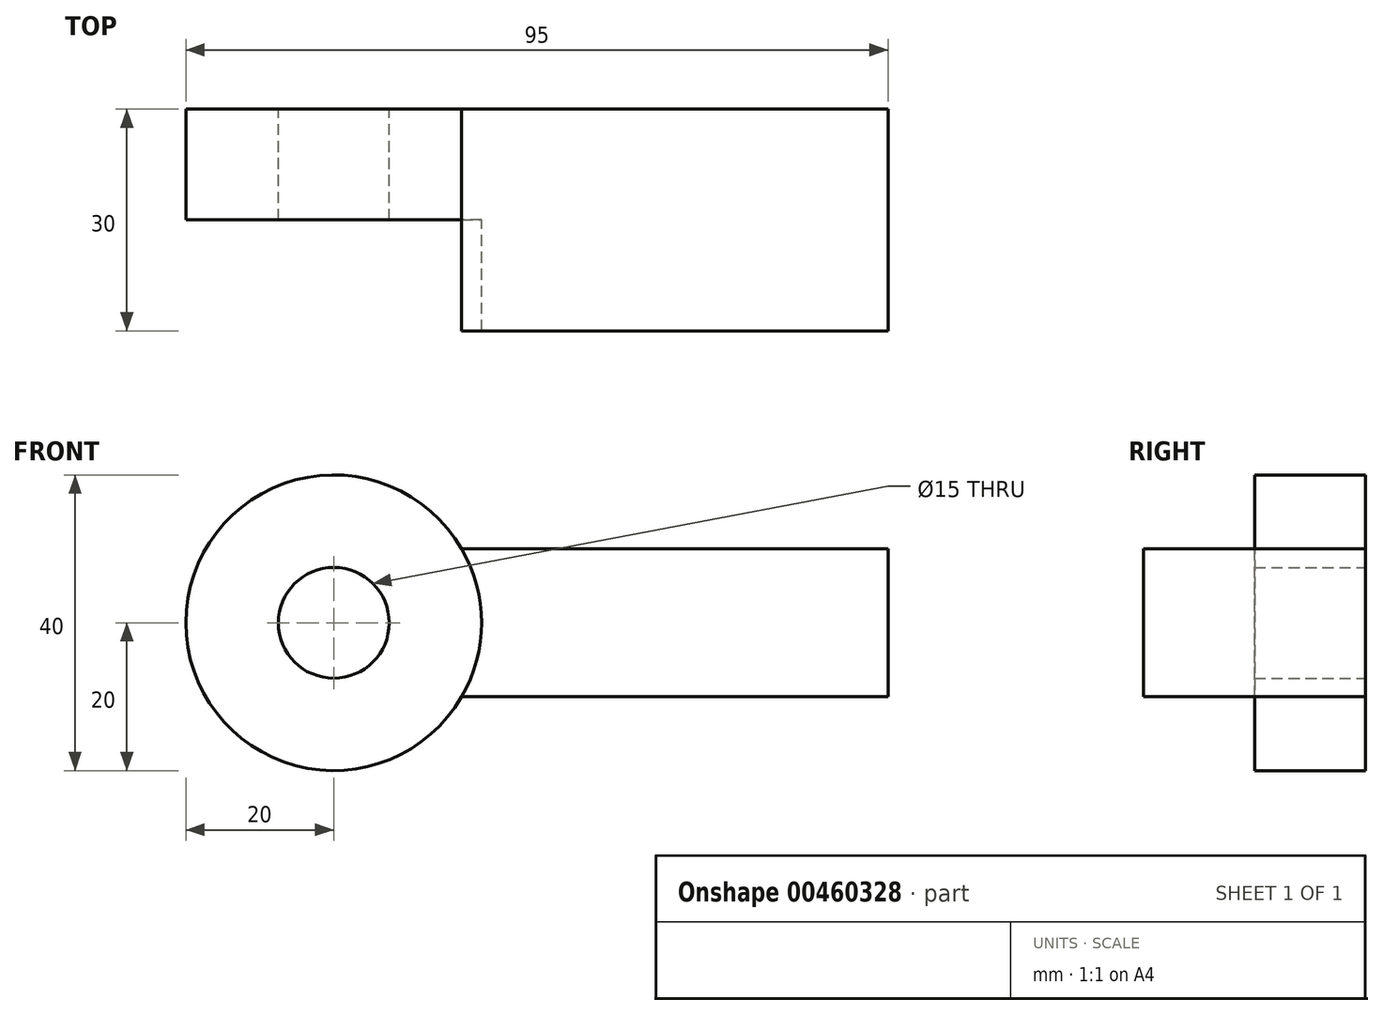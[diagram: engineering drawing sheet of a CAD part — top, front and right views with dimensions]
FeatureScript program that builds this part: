
annotation { "Feature Type Name" : "Feature", "Feature Type Description" : "" }
export const myFeature = defineFeature(function(context is Context, id is Id, definition is map)
    precondition{}
    {
        {
            var Q0;
            Q0=qCreatedBy(makeId("Front.planeOp"),FACE);
            var sketch = newSketch(context, id + "F0", { "sketchPlane" : qUnion([Q0])});
            skCircle(sketch, "E0", {"center": v(-20, 0) * mm, "radius": 20 * mm});
            skCircle(sketch, "E1", {"center": v(-20, 0) * mm, "radius": 7.5 * mm});
            skLineSegment(sketch, "E2", {"start": v(-2.68, 10) * mm, "end": v(55, 10) * mm});
            skLineSegment(sketch, "E3", {"start": v(55, 10) * mm, "end": v(55, -10) * mm});
            skLineSegment(sketch, "E4", {"start": v(55, -10) * mm, "end": v(-2.68, -10) * mm});
            skSolve(sketch);
        }
        {
            var Q0;
            Q0=makeQuery(id+"F0.imprint","IMPRINT",FACE,{"disambiguationData":[TD([[makeQuery(id+"F0.imprint","IMPRINT",EDGE,{"derivedFrom":sQuery(id+"F0.wireOp",EDGE,"E0")}),1.0]])]});
            extrude(context, id + "F1", {"entities" : qUnion([Q0]), "depth" : 15 * mm});
        }
        {
            var Q0;
            {var subQ0=sQuery(id+"F0.wireOp",EDGE,"E2");Q0=makeQuery(id+"F0.imprint","IMPRINT",FACE,{"disambiguationData":[TD([[makeQuery(id+"F0.imprint","IMPRINT",EDGE,{"derivedFrom":subQ0}),-1.0]])]});}
            extrude(context, id + "F2", {"entities" : qUnion([Q0]), "operationType" : NewBodyOperationType.ADD, "depth" : 30 * mm});
        }
    });
